SOLIDWORKS PART (.sldprt)
format: sldprt  version: not decoded by parser v0  size: 86,528 bytes
history: native  units: mm
features: sketch x3, extrude x2, material x1, cut_extrude x1, pattern_circular x1 (+16 scaffold rows collapsed)
feature tree (24):
  scaffold x16  (default folders/planes/origin — collapsed)
  material  "Material <not specified>"
  sketch  "Sketch1"  dims[D1=30.0mm D2=16.0mm]
  extrude  "Boss-Extrude1"  Depth=80mm
  sketch  "Sketch2"  dims[D1=100.0mm]
  extrude  "Boss-Extrude2"  Depth=8mm
  sketch  "Sketch3"  dims[D1=5.0mm D2=40.0mm]
  cut_extrude  "Cut-Extrude1"  Depth=8mm
  pattern_circular  "CirPattern1"  Count=3 Angle=120deg
decode coverage: 7 of 7 modeling features carry decoded parameters
note: suppression state not decoded; provenance and decode notes live in map.json
